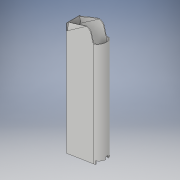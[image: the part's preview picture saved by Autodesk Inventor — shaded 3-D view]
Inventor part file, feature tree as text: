
AUTODESK INVENTOR PART (.ipt)
format: ipt  version: 2018.3 (Build 223284000, 284)  size: 329,216 bytes
history: native  units: in
note: dims shown in document units (in); Inventor stores cm internally (conversion verified against a paired STEP export)
features: sketch x8, extrude x5, plane x4, split x3, other x2, boolean_combine x1
ambient origin geometry x8: Origin, YZ Plane, XZ Plane, XY Plane, X Axis, Y Axis, Z Axis, Center Point
bodies: Solid1 (feature_tree), Solid2 (feature_tree), Solid3 (feature_tree), Solid4 (feature_tree), Solid5 (feature_tree), Solid6 (feature_tree), Solid7 (feature_tree)
feature tree (23):
  sketch  "Sketch1"  dims[d0=0.541in d1=0.2445in]
  extrude  "Extrusion1"  Depth=0.2445in
  sketch  "Sketch3"  dims[d2=0.026in d3=0.026in]
  sketch  "Sketch4"  dims[d4=0.026in d5=0.015in]
  extrude  "Extrusion2"  Depth=0.026in
  plane  "Work Plane1"
  extrude  "Extrusion3"  Depth=0.015in
  extrude  "Extrusion4"  Depth=0.81in
  plane  "Work Plane2"
  extrude  "Extrusion5"  Depth=0.8in
  sketch  "Sketch8"  dims[d11=0.4in]
  split  "Split1"
  split  "Split2"
  split  "Split3"
  plane  "Work Plane4"
  other  "Bend Part1"
  plane  "Work Plane5"
  other  "Bend Part2"
  boolean_combine  "Combine1"
  sketch  "Sketch5"  dims[d6=4.82in d7=0.0in d8=0.81in]
  sketch  "Sketch6"  dims[d9=0.9in d10=0.8in]
  sketch  "Sketch10"  dims[d12=0.0618in]
  sketch  "Sketch11"  dims[d13=0.125in d14=1.172in d15=1.372in d16=1.372in d17=4.4761in d18=0.3439in d19=3.0in d20=0.0in d23=0.125in d24=0.0in d25=4.005in d26=105.0deg d27=1.0994in d28=0.05in d29=1.0in d30=0.0in d31=2.0in d32=0.0in d33=0.0in d35=0.0in d36=0.5in d37=0.5497in d38=0.0in d39=0.5in d40=0.5497in]
